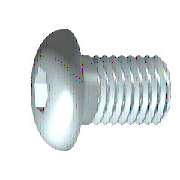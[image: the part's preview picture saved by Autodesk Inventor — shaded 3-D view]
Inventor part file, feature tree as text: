
AUTODESK INVENTOR PART (.ipt)
format: ipt  version: 2013 (Build 170138000, 138)  size: 189,440 bytes
history: native  units: mm (DEFAULTED — no unit token found)
features: sketch x2, extrude x1, plane x1, fillet x1
ambient origin geometry x7: Origin, YZ Plane, XY Plane, X Axis, Y Axis, Z Axis, Center Point
bodies: Solid1 (feature_tree), Body (feature_tree)
feature tree (5):
  extrude  "Slot"  Depth=1.59014mm
  plane  "Work Plane1"
  fillet  "Fillet2"  Radius=2.2098mm
  sketch  "Sketch1"  dims[d1=17.45976mm d2=1.59014mm d3=2.2098mm]
  sketch  "Sketch2"  dims[d4=1.3208mm d5=60.0deg d6=4.1656mm d7=4.1656mm d8=2.756963mm d9=7.9248mm d10=90.0deg d11=10.0mm d12=0.0mm d13=17.45976mm d14=0.0mm d15=0.486918mm d16=0.486918mm d17=1.9558mm d19=0.0mm d26=19.05mm d27=45.0deg d28=0.0mm d29=0.0mm d30=0.1mm]
